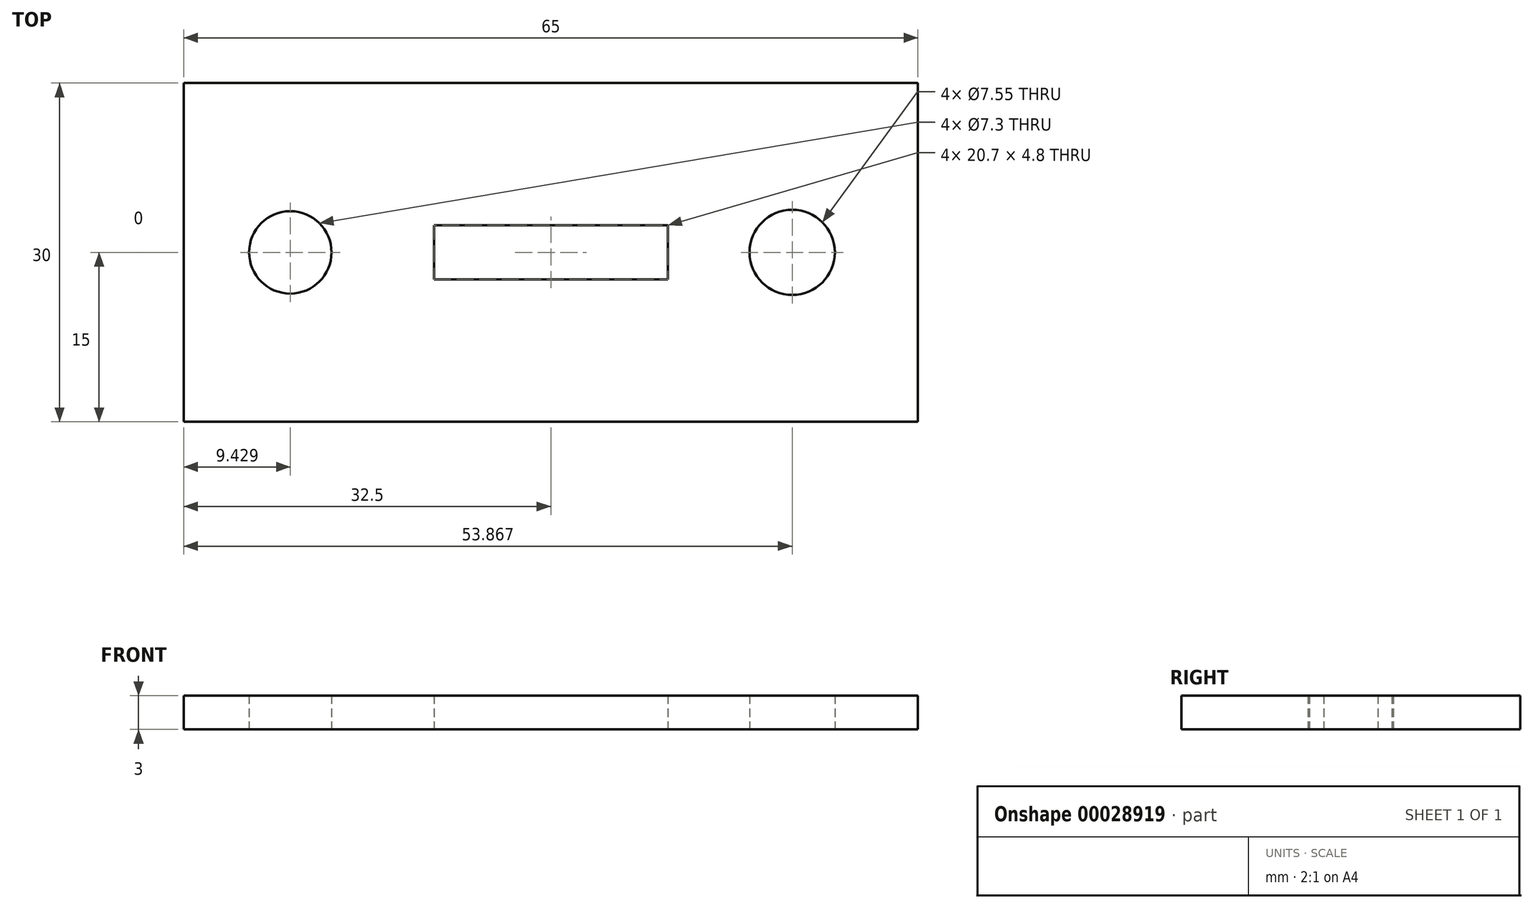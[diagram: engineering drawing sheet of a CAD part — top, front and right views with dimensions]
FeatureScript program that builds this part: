
annotation { "Feature Type Name" : "Feature", "Feature Type Description" : "" }
export const myFeature = defineFeature(function(context is Context, id is Id, definition is map)
    precondition{}
    {
        {
            var Q0;
            Q0=qCreatedBy(makeId("Top.planeOp"),FACE);
            var sketch = newSketch(context, id + "F0", { "sketchPlane" : qUnion([Q0])});
            skLineSegment(sketch, "E0.rect.bottom", {"start": v(10.35, 2.4) * mm, "end": v(-10.35, 2.4) * mm});
            skLineSegment(sketch, "E0.rect.top", {"start": v(10.35, -2.4) * mm, "end": v(-10.35, -2.4) * mm});
            skLineSegment(sketch, "E0.rect.left", {"start": v(10.35, 2.4) * mm, "end": v(10.35, -2.4) * mm});
            skLineSegment(sketch, "E0.rect.right", {"start": v(-10.35, 2.4) * mm, "end": v(-10.35, -2.4) * mm});
            skPoint(sketch, "E0.rect.middle", {"position": v(0, 0) * mm});
            skLineSegment(sketch, "E1.rect.bottom", {"start": v(32.5, 15) * mm, "end": v(-32.5, 15) * mm});
            skLineSegment(sketch, "E1.rect.top", {"start": v(32.5, -15) * mm, "end": v(-32.5, -15) * mm});
            skLineSegment(sketch, "E1.rect.left", {"start": v(32.5, 15) * mm, "end": v(32.5, -15) * mm});
            skLineSegment(sketch, "E1.rect.right", {"start": v(-32.5, 15) * mm, "end": v(-32.5, -15) * mm});
            skCircle(sketch, "E2", {"center": v(-23.07, 0) * mm, "radius": 3.65 * mm});
            skCircle(sketch, "E3", {"center": v(21.37, 0) * mm, "radius": 3.77 * mm});
            skSolve(sketch);
        }
        {
            var Q0;
            Q0=makeQuery(id+"F0.imprint","IMPRINT",FACE,{"disambiguationData":[TD([[makeQuery(id+"F0.imprint","IMPRINT",EDGE,{"derivedFrom":sQuery(id+"F0.wireOp",EDGE,"E0.rect.bottom")}),-1.0]])]});
            extrude(context, id + "F1", {"entities" : qUnion([Q0]), "depth" : 3 * mm});
        }
    });
